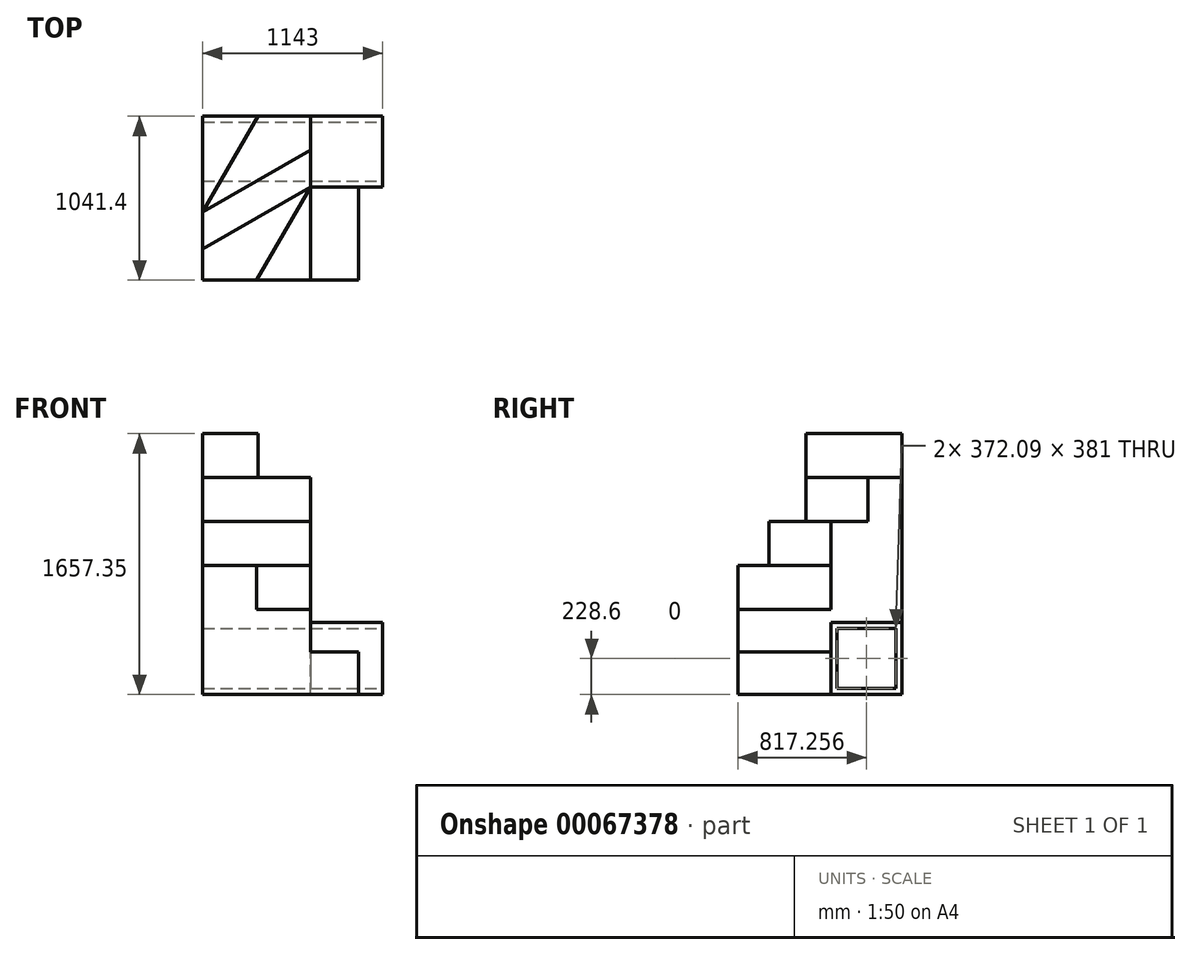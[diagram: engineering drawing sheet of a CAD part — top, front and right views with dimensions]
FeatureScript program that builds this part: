
annotation { "Feature Type Name" : "Feature", "Feature Type Description" : "" }
export const myFeature = defineFeature(function(context is Context, id is Id, definition is map)
    precondition{}
    {
        {
            var Q0;
            Q0=qCreatedBy(makeId("Top.planeOp"),FACE);
            var sketch = newSketch(context, id + "F0", { "sketchPlane" : qUnion([Q0])});
            skLineSegment(sketch, "E0.bottom", {"start": v(0, 0) * mm, "end": v(685.8, 0) * mm});
            skLineSegment(sketch, "E0.top", {"start": v(0, -1041.4) * mm, "end": v(685.8, -1041.4) * mm});
            skLineSegment(sketch, "E0.left", {"start": v(0, 0) * mm, "end": v(0, -1041.4) * mm});
            skLineSegment(sketch, "E0.right", {"start": v(685.8, 0) * mm, "end": v(685.8, -1041.4) * mm});
            skLineSegment(sketch, "E1.bottom", {"start": v(0, -1041.4) * mm, "end": v(685.8, -1041.4) * mm, "construction": true});
            skLineSegment(sketch, "E1.top", {"start": v(0, -2260.6) * mm, "end": v(685.8, -2260.6) * mm, "construction": true});
            skLineSegment(sketch, "E1.left", {"start": v(0, -1041.4) * mm, "end": v(0, -2260.6) * mm, "construction": true});
            skLineSegment(sketch, "E1.right", {"start": v(685.8, -1041.4) * mm, "end": v(685.8, -2260.6) * mm, "construction": true});
            skSolve(sketch);
        }
        {
            var Q0;
            Q0 = qSketchRegion(id + "F0", true);
            extrude(context, id + "F1", {"entities" : qUnion([Q0]), "depth" : 1657.35 * mm});
        }
        {
            var Q0;
            Q0=makeQuery(id+"F1.opExtrude","CAP_FACE",FACE,{"disambiguationData":[OSD([sQuery(id+"F0.wireOp",EDGE,"E0.bottom"),sQuery(id+"F0.wireOp",EDGE,"E0.top"),sQuery(id+"F0.wireOp",EDGE,"E0.left"),sQuery(id+"F0.wireOp",EDGE,"E0.right")])],"isStart":false});
            var sketch = newSketch(context, id + "F2", { "sketchPlane" : qUnion([Q0])});
            skLineSegment(sketch, "E2", {"start": v(0, -609.6) * mm, "end": v(351.95, 0) * mm});
            skLineSegment(sketch, "E3", {"start": v(351.95, 0) * mm, "end": v(685.8, 0) * mm});
            skLineSegment(sketch, "E4", {"start": v(685.8, 0) * mm, "end": v(685.8, -1041.4) * mm});
            skLineSegment(sketch, "E5", {"start": v(685.8, -1041.4) * mm, "end": v(0, -1041.4) * mm});
            skLineSegment(sketch, "E6", {"start": v(0, -1041.4) * mm, "end": v(0, -609.6) * mm});
            skSolve(sketch);
        }
        {
            var Q0;
            Q0 = qSketchRegion(id + "F2", true);
            extrude(context, id + "F3", {"entities" : qUnion([Q0]), "operationType" : NewBodyOperationType.REMOVE, "oppositeDirection" : true, "depth" : 279.4 * mm});
        }
        {
            var Q0;
            Q0=makeQuery(id+"F3.boolean.opBoolean","COPY",FACE,{"derivedFrom":makeQuery(id+"F3.opExtrude","CAP_FACE",FACE,{"disambiguationData":[OSD([sQuery(id+"F2.wireOp",EDGE,"E2"),sQuery(id+"F2.wireOp",EDGE,"E3"),sQuery(id+"F2.wireOp",EDGE,"E4"),sQuery(id+"F2.wireOp",EDGE,"E5"),sQuery(id+"F2.wireOp",EDGE,"E6")])],"isStart":false})});
            var sketch = newSketch(context, id + "F4", { "sketchPlane" : qUnion([Q0])});
            skLineSegment(sketch, "E7", {"start": v(0, -1041.4) * mm, "end": v(0, -609.6) * mm});
            skLineSegment(sketch, "E8", {"start": v(0, -609.6) * mm, "end": v(685.8, -213.65) * mm});
            skLineSegment(sketch, "E9", {"start": v(685.8, -213.65) * mm, "end": v(685.8, -1041.4) * mm});
            skLineSegment(sketch, "E10", {"start": v(685.8, -1041.4) * mm, "end": v(0, -1041.4) * mm});
            skSolve(sketch);
        }
        {
            var Q0;
            Q0 = qSketchRegion(id + "F4", true);
            extrude(context, id + "F5", {"entities" : qUnion([Q0]), "operationType" : NewBodyOperationType.REMOVE, "oppositeDirection" : true, "depth" : 279.4 * mm});
        }
        {
            var Q0;
            Q0=makeQuery(id+"F5.boolean.opBoolean","COPY",FACE,{"derivedFrom":makeQuery(id+"F5.opExtrude","CAP_FACE",FACE,{"disambiguationData":[OSD([sQuery(id+"F4.wireOp",EDGE,"E7"),sQuery(id+"F4.wireOp",EDGE,"E8"),sQuery(id+"F4.wireOp",EDGE,"E9"),sQuery(id+"F4.wireOp",EDGE,"E10")])],"isStart":false})});
            var sketch = newSketch(context, id + "F6", { "sketchPlane" : qUnion([Q0])});
            skLineSegment(sketch, "E11", {"start": v(0, -844.24) * mm, "end": v(685.8, -448.29) * mm});
            skLineSegment(sketch, "E12", {"start": v(685.8, -448.29) * mm, "end": v(685.8, -1041.4) * mm});
            skLineSegment(sketch, "E13", {"start": v(685.8, -1041.4) * mm, "end": v(0, -1041.4) * mm});
            skLineSegment(sketch, "E14", {"start": v(0, -1041.4) * mm, "end": v(0, -844.24) * mm});
            skSolve(sketch);
        }
        {
            var Q0;
            Q0 = qSketchRegion(id + "F6", true);
            extrude(context, id + "F7", {"entities" : qUnion([Q0]), "operationType" : NewBodyOperationType.REMOVE, "oppositeDirection" : true, "depth" : 279.4 * mm});
        }
        {
            var Q0;
            Q0=makeQuery(id+"F7.boolean.opBoolean","COPY",FACE,{"derivedFrom":makeQuery(id+"F7.opExtrude","CAP_FACE",FACE,{"disambiguationData":[OSD([sQuery(id+"F6.wireOp",EDGE,"E11"),sQuery(id+"F6.wireOp",EDGE,"E12"),sQuery(id+"F6.wireOp",EDGE,"E13"),sQuery(id+"F6.wireOp",EDGE,"E14")])],"isStart":false})});
            var sketch = newSketch(context, id + "F8", { "sketchPlane" : qUnion([Q0])});
            skLineSegment(sketch, "E15.bottom", {"start": v(343.37, -1041.4) * mm, "end": v(685.8, -448.29) * mm});
            skLineSegment(sketch, "E15.top", {"start": v(343.37, -1041.4) * mm, "end": v(685.8, -1041.4) * mm});
            skLineSegment(sketch, "E15.right", {"start": v(685.8, -448.29) * mm, "end": v(685.8, -1041.4) * mm});
            skSolve(sketch);
        }
        {
            var Q0;
            Q0 = qSketchRegion(id + "F8", true);
            extrude(context, id + "F9", {"entities" : qUnion([Q0]), "operationType" : NewBodyOperationType.REMOVE, "oppositeDirection" : true, "depth" : 279.4 * mm});
        }
        {
            var Q0;
            Q0=makeQuery(id+"F1.opExtrude","SWEPT_FACE",FACE,{"disambiguationData":[OSD([sQuery(id+"F0.wireOp",EDGE,"E0.right")])]});
            var sketch = newSketch(context, id + "F10", { "sketchPlane" : qUnion([Q0])});
            skLineSegment(sketch, "E16.bottom", {"start": v(-1041.4, 0) * mm, "end": v(-448.29, 0) * mm});
            skLineSegment(sketch, "E16.top", {"start": v(-1041.4, 269.87) * mm, "end": v(-448.29, 269.87) * mm});
            skLineSegment(sketch, "E16.left", {"start": v(-1041.4, 0) * mm, "end": v(-1041.4, 269.87) * mm});
            skLineSegment(sketch, "E16.right", {"start": v(-448.29, 0) * mm, "end": v(-448.29, 269.87) * mm});
            skLineSegment(sketch, "E17", {"start": v(-448.29, 269.87) * mm, "end": v(-448.29, 539.75) * mm, "construction": true});
            skSolve(sketch);
        }
        {
            var Q0;
            Q0 = qSketchRegion(id + "F10", true);
            extrude(context, id + "F11", {"entities" : qUnion([Q0]), "operationType" : NewBodyOperationType.ADD, "depth" : 304.8 * mm});
        }
        {
            var Q0;
            Q0=makeQuery(id+"F1.opExtrude","SWEPT_FACE",FACE,{"disambiguationData":[OSD([sQuery(id+"F0.wireOp",EDGE,"E0.right")])]});
            var sketch = newSketch(context, id + "F12", { "sketchPlane" : qUnion([Q0])});
            skLineSegment(sketch, "E18.bottom", {"start": v(0, 0) * mm, "end": v(-448.29, 0) * mm});
            skLineSegment(sketch, "E18.top", {"start": v(0, 457.2) * mm, "end": v(-448.29, 457.2) * mm});
            skLineSegment(sketch, "E18.left", {"start": v(0, 0) * mm, "end": v(0, 457.2) * mm});
            skLineSegment(sketch, "E18.right", {"start": v(-448.29, 0) * mm, "end": v(-448.29, 457.2) * mm});
            skSolve(sketch);
        }
        {
            var Q0;
            Q0 = qSketchRegion(id + "F12", true);
            extrude(context, id + "F13", {"entities" : qUnion([Q0]), "depth" : 457.2 * mm});
        }
        {
            var Q0;
            Q0=makeQuery(id+"F13.opExtrude","CAP_FACE",FACE,{"disambiguationData":[OSD([sQuery(id+"F12.wireOp",EDGE,"E18.bottom"),sQuery(id+"F12.wireOp",EDGE,"E18.top"),sQuery(id+"F12.wireOp",EDGE,"E18.left"),sQuery(id+"F12.wireOp",EDGE,"E18.right")])],"isStart":false});
            var sketch = newSketch(context, id + "F14", { "sketchPlane" : qUnion([Q0])});
            skLineSegment(sketch, "E19.bottom", {"start": v(-410.19, 419.1) * mm, "end": v(-38.1, 419.1) * mm});
            skLineSegment(sketch, "E19.top", {"start": v(-410.19, 38.1) * mm, "end": v(-38.1, 38.1) * mm});
            skLineSegment(sketch, "E19.left", {"start": v(-410.19, 419.1) * mm, "end": v(-410.19, 38.1) * mm});
            skLineSegment(sketch, "E19.right", {"start": v(-38.1, 419.1) * mm, "end": v(-38.1, 38.1) * mm});
            skLineSegment(sketch, "E20", {"start": v(-38.1, 228.6) * mm, "end": v(0, 228.6) * mm, "construction": true});
            skLineSegment(sketch, "E21", {"start": v(-224.14, 419.1) * mm, "end": v(-224.14, 457.2) * mm, "construction": true});
            skLineSegment(sketch, "E22", {"start": v(-410.19, 228.6) * mm, "end": v(-448.29, 228.6) * mm, "construction": true});
            skLineSegment(sketch, "E23", {"start": v(-224.14, 38.1) * mm, "end": v(-224.14, 0) * mm, "construction": true});
            skSolve(sketch);
        }
        {
            var Q0;
            Q0 = qSketchRegion(id + "F14", true);
            extrude(context, id + "F15", {"entities" : qUnion([Q0]), "operationType" : NewBodyOperationType.REMOVE, "endBound" : BoundingType.THROUGH_ALL, "oppositeDirection" : true, "depth" : 25.4 * mm});
        }
    });
